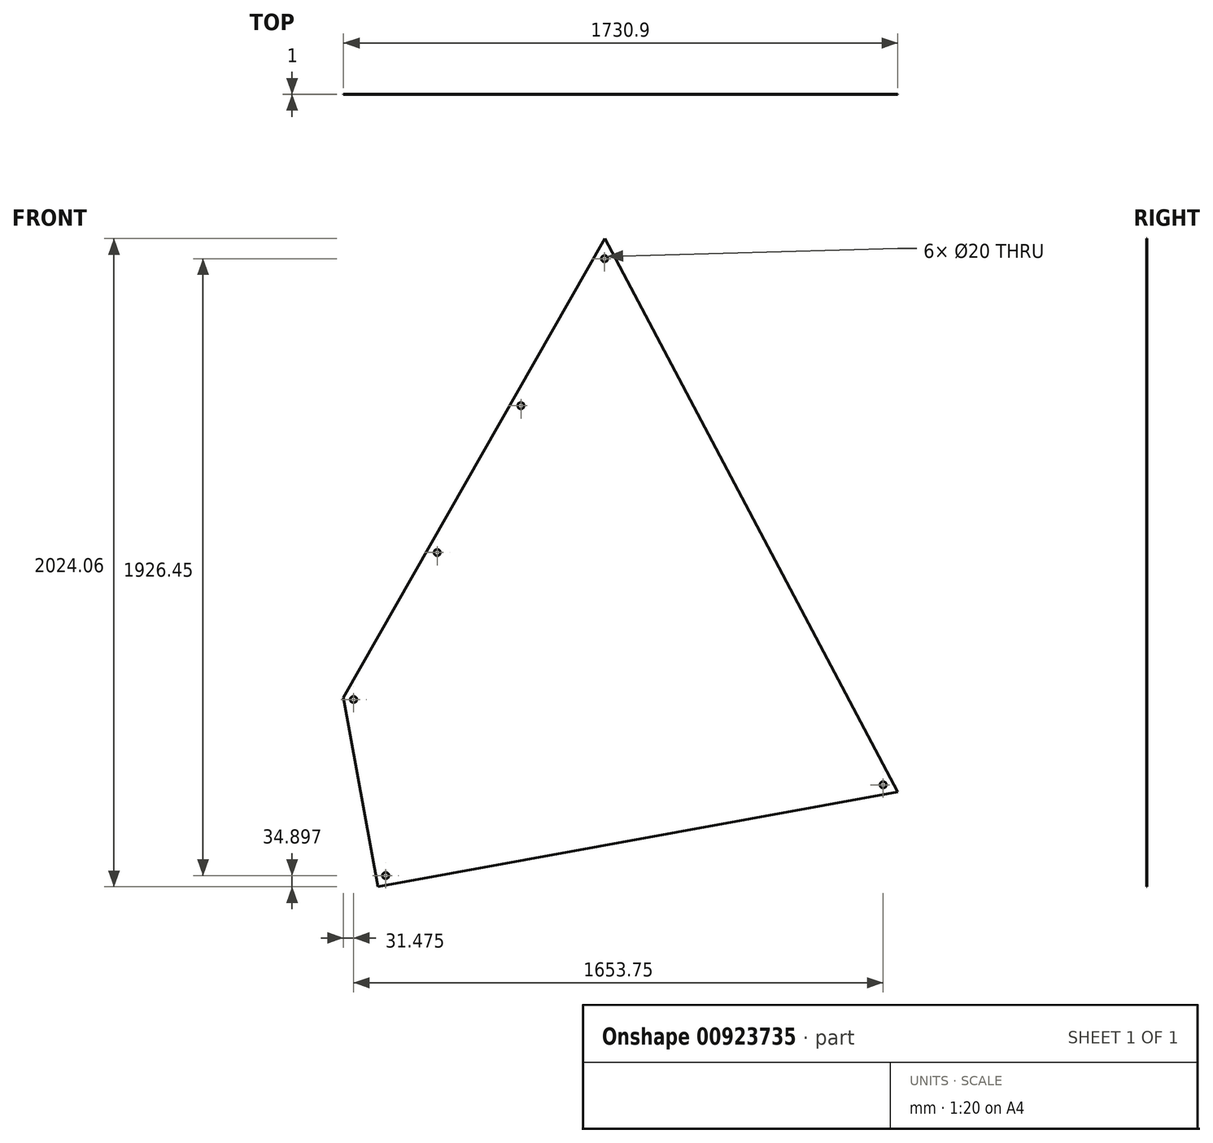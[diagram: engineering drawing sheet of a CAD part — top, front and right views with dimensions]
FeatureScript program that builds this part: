
annotation { "Feature Type Name" : "Feature", "Feature Type Description" : "" }
export const myFeature = defineFeature(function(context is Context, id is Id, definition is map)
    precondition{}
    {
        {
            var Q0;
            Q0=qCreatedBy(makeId("Front.planeOp"),FACE);
            var sketch = newSketch(context, id + "F0", { "sketchPlane" : qUnion([Q0])});
            skLineSegment(sketch, "E0", {"start": v(0, 0) * mm, "end": v(-107.69, 590.26) * mm});
            skLineSegment(sketch, "E1", {"start": v(-107.69, 590.26) * mm, "end": v(708.83, 2024.06) * mm});
            skLineSegment(sketch, "E2", {"start": v(708.83, 2024.06) * mm, "end": v(1623.2, 296.14) * mm});
            skLineSegment(sketch, "E3", {"start": v(1623.2, 296.14) * mm, "end": v(0, 0) * mm});
            skSolve(sketch);
        }
        {
            var Q0;
            Q0 = qSketchRegion(id + "F0", true);
            extrude(context, id + "F1", {"entities" : qUnion([Q0]), "depth" : 1 * mm, "offsetDistance" : 25 * mm});
        }
        {
            var Q0;
            Q0=makeQuery(id+"F1.opExtrude","CAP_FACE",FACE,{"disambiguationData":[OSD([sQuery(id+"F0.wireOp",EDGE,"E0"),sQuery(id+"F0.wireOp",EDGE,"E1"),sQuery(id+"F0.wireOp",EDGE,"E2"),sQuery(id+"F0.wireOp",EDGE,"E3")])],"isStart":false});
            var sketch = newSketch(context, id + "F2", { "sketchPlane" : qUnion([Q0])});
            skCircle(sketch, "E4", {"center": v(-76.22, 584.9) * mm, "radius": 10 * mm});
            skCircle(sketch, "E5.1.0.0", {"center": v(185.07, 1043.72) * mm, "radius": 10 * mm});
            skCircle(sketch, "E5.2.0.0", {"center": v(446.36, 1502.53) * mm, "radius": 10 * mm});
            skCircle(sketch, "E5.3.0.0", {"center": v(707.64, 1961.35) * mm, "radius": 10 * mm});
            skLineSegment(sketch, "E5.direction1", {"start": v(-76.22, 584.9) * mm, "end": v(185.07, 1043.72) * mm, "construction": true});
            skLineSegment(sketch, "E6.0.2", {"start": v(708.83, 2024.06) * mm, "end": v(-107.69, 590.26) * mm, "construction": true});
            skCircle(sketch, "E7", {"center": v(24.13, 34.9) * mm, "radius": 10 * mm});
            skCircle(sketch, "E8", {"center": v(1577.54, 318.3) * mm, "radius": 10 * mm});
            skSolve(sketch);
        }
        {
            var Q0;
            Q0 = qSketchRegion(id + "F2", true);
            extrude(context, id + "F3", {"entities" : qUnion([Q0]), "operationType" : NewBodyOperationType.REMOVE, "endBound" : BoundingType.THROUGH_ALL, "oppositeDirection" : true, "depth" : 25 * mm, "offsetDistance" : 25 * mm});
        }
    });
